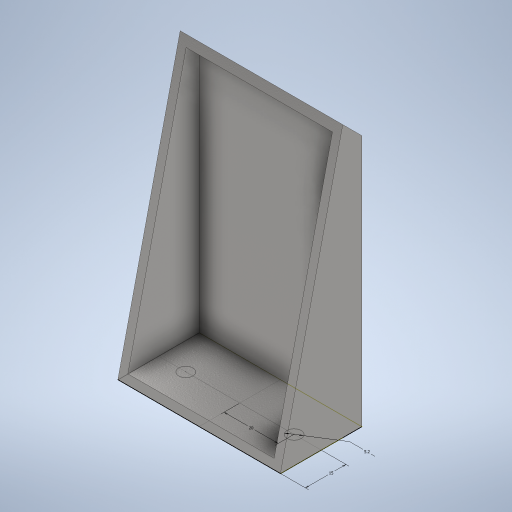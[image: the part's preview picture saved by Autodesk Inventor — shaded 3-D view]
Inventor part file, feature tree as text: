
AUTODESK INVENTOR PART (.ipt)
format: ipt  version: 2024.2 (Build 282272000, 272)  size: 272,384 bytes
history: native  units: mm
features: sketch x3, extrude x2, chamfer x1, shell x1
ambient origin geometry x8: Origin, YZ Plane, XZ Plane, XY Plane, X Axis, Y Axis, Z Axis, Center Point
bodies: Body1 (feature_tree)
feature tree (7):
  extrude  "Extrusion4"  Depth=30.0mm
  chamfer  "Chamfer1"  Distance=100.0mm
  extrude  "Extrusion5"  Depth=3.0mm TaperAngle=0.0deg
  shell  "Shell2"  Thickness=3.0mm
  sketch  "Sketch8"  dims[d26=15.0mm d27=20.0mm d28=5.2mm d3=0.5mm d4=0.872665mm d5=0.5mm d6=0.872665mm d29=0.872665mm]
  sketch  "Sketch4"  dims[d15=60.0mm d16=30.0mm d17=100.0mm d18=0.0mm]
  sketch  "Sketch6"  dims[d19=7.0mm d20=2.0mm d21=45.0deg d22=100.0mm d23=0.0mm d25=3.0mm]
